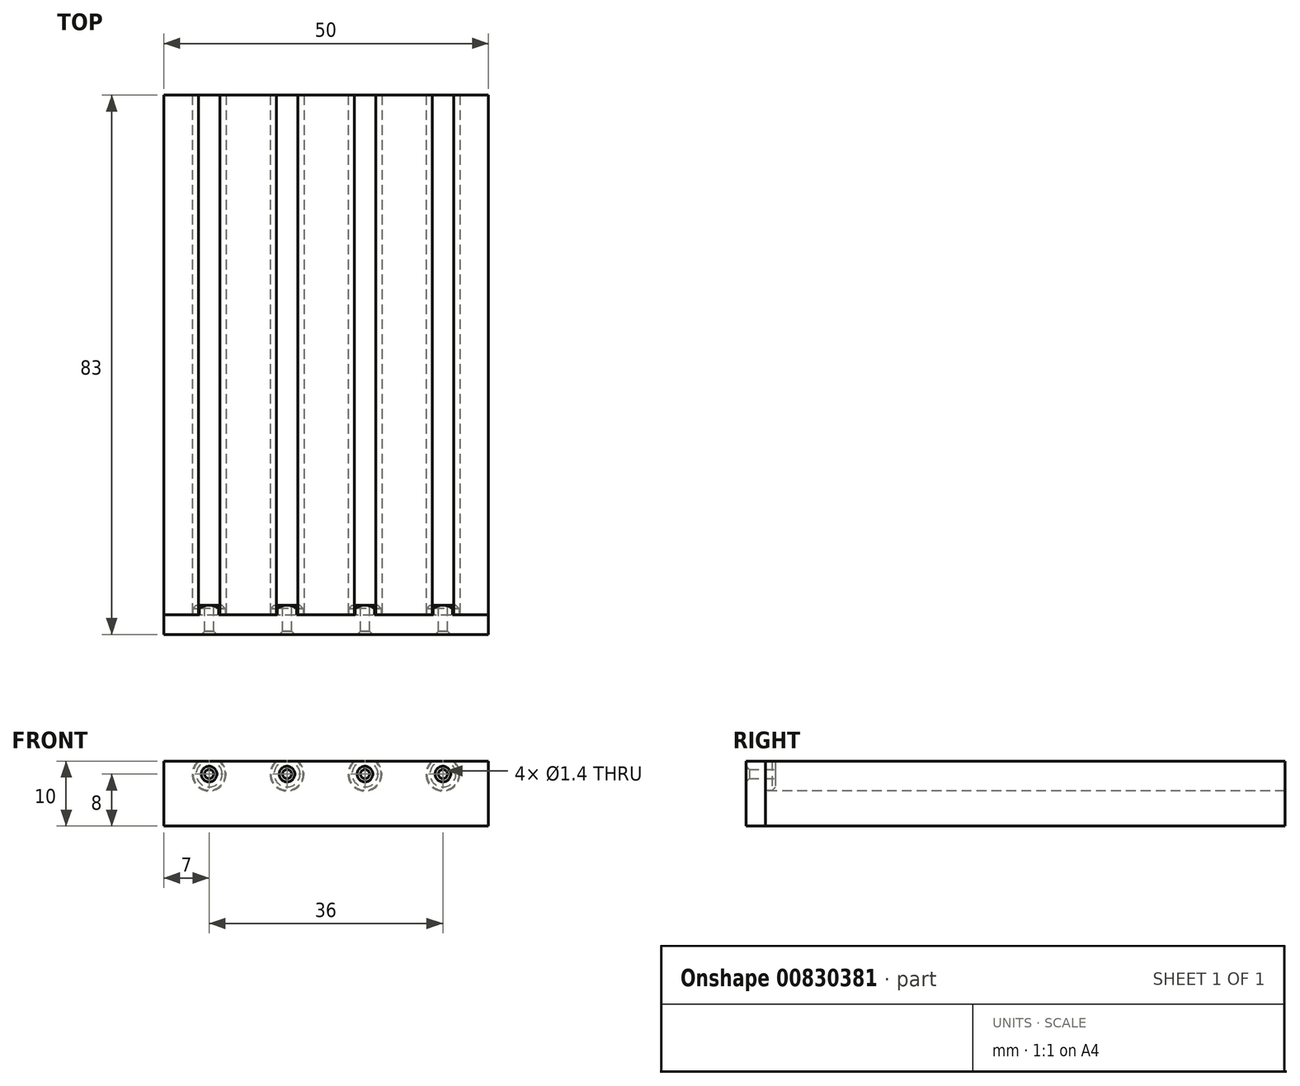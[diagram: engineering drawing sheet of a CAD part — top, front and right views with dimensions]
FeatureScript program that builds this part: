
annotation { "Feature Type Name" : "Feature", "Feature Type Description" : "" }
export const myFeature = defineFeature(function(context is Context, id is Id, definition is map)
    precondition{}
    {
        {
            var Q0;
            Q0=qCreatedBy(makeId("Top.planeOp"),FACE);
            var sketch = newSketch(context, id + "F0", { "sketchPlane" : qUnion([Q0]), "disableImprinting" : false});
            skLineSegment(sketch, "E0.bottom", {"start": v(25, 40) * mm, "end": v(-25, 40) * mm});
            skLineSegment(sketch, "E0.top", {"start": v(25, -40) * mm, "end": v(-25, -40) * mm});
            skLineSegment(sketch, "E0.left", {"start": v(25, 40) * mm, "end": v(25, -40) * mm});
            skLineSegment(sketch, "E0.right", {"start": v(-25, 40) * mm, "end": v(-25, -40) * mm});
            skPoint(sketch, "E0.middle", {"position": v(0, 0) * mm});
            skLineSegment(sketch, "E1.bottom", {"start": v(-25, -38.5) * mm, "end": v(25, -38.5) * mm});
            skLineSegment(sketch, "E1.top", {"start": v(-25, -43) * mm, "end": v(25, -43) * mm});
            skLineSegment(sketch, "E1.left", {"start": v(-25, -38.5) * mm, "end": v(-25, -43) * mm});
            skLineSegment(sketch, "E1.right", {"start": v(25, -38.5) * mm, "end": v(25, -43) * mm});
            skSolve(sketch);
        }
        {
            var Q0;
            Q0=makeQuery(id+"F0.imprint","IMPRINT",FACE,{"disambiguationData":[TD([[makeQuery(id+"F0.imprint","IMPRINT",EDGE,{"derivedFrom":sQuery(id+"F0.wireOp",EDGE,"E0.bottom")}),1.0]])]});
            var Q1;
            {var subQ0=sQuery(id+"F0.wireOp",EDGE,"E0.top");Q1=makeQuery(id+"F0.imprint","IMPRINT",FACE,{"disambiguationData":[TD([[makeQuery(id+"F0.imprint","IMPRINT",EDGE,{"derivedFrom":subQ0}),-1.0]])]});}
            extrude(context, id + "F1", {"entities" : qUnion([Q0, Q1]), "depth" : 10 * mm, "offsetDistance" : 25 * mm});
        }
        {
            var Q0;
            Q0=makeQuery(id+"F1.opExtrude","SWEPT_FACE",FACE,{"disambiguationData":[OSD([sQuery(id+"F0.wireOp",EDGE,"E0.top")])]});
            var sketch = newSketch(context, id + "F2", { "sketchPlane" : qUnion([Q0]), "disableImprinting" : false});
            skLineSegment(sketch, "E2.0.0", {"start": v(-25, 0) * mm, "end": v(25, 0) * mm});
            skLineSegment(sketch, "E2.0.1", {"start": v(25, 0) * mm, "end": v(25, 10) * mm});
            skLineSegment(sketch, "E2.0.2", {"start": v(25, 10) * mm, "end": v(-25, 10) * mm});
            skLineSegment(sketch, "E2.0.3", {"start": v(-25, 10) * mm, "end": v(-25, 0) * mm});
            skLineSegment(sketch, "E3", {"start": v(-27.18, 8) * mm, "end": v(25, 8) * mm, "construction": true});
            skCircle(sketch, "E4", {"center": v(-18, 8) * mm, "radius": 2.6 * mm});
            skCircle(sketch, "E5.1.0.0", {"center": v(-6, 8) * mm, "radius": 2.6 * mm});
            skCircle(sketch, "E5.2.0.0", {"center": v(6, 8) * mm, "radius": 2.6 * mm});
            skCircle(sketch, "E5.3.0.0", {"center": v(18, 8) * mm, "radius": 2.6 * mm});
            skLineSegment(sketch, "E5.direction1", {"start": v(-18, 8) * mm, "end": v(-6, 8) * mm, "construction": true});
            skLineSegment(sketch, "E6", {"start": v(0, 10) * mm, "end": v(0, 0) * mm, "construction": true});
            skSolve(sketch);
        }
        {
            var Q0;
            {var subQ0=sQuery(id+"F2.wireOp",EDGE,"E5.5.0.0");var subQ1=sQuery(id+"F2.wireOp",EDGE,"E2.0.2");var subQ2=makeQuery(id+"F2.imprint","INTERSECT",VERTEX,{"disambiguationData":[OD(0.0)],"derivedFrom":[subQ1,subQ0]});Q0=makeQuery(id+"F2.imprint","IMPRINT",FACE,{"disambiguationData":[TD([[makeQuery(id+"F2.imprint","IMPRINT",EDGE,{"disambiguationData":[TD([[subQ2,-1.0]])],"derivedFrom":subQ1}),-1.0]])]});}
            var Q1;
            {var subQ0=sQuery(id+"F2.wireOp",EDGE,"E5.4.0.0");var subQ1=sQuery(id+"F2.wireOp",EDGE,"E2.0.2");var subQ2=makeQuery(id+"F2.imprint","INTERSECT",VERTEX,{"disambiguationData":[OD(0.0)],"derivedFrom":[subQ1,subQ0]});Q1=makeQuery(id+"F2.imprint","IMPRINT",FACE,{"disambiguationData":[TD([[makeQuery(id+"F2.imprint","IMPRINT",EDGE,{"disambiguationData":[TD([[subQ2,-1.0]])],"derivedFrom":subQ1}),-1.0]])]});}
            var Q2;
            {var subQ0=sQuery(id+"F2.wireOp",EDGE,"E5.3.0.0");var subQ1=sQuery(id+"F2.wireOp",EDGE,"E2.0.2");var subQ2=makeQuery(id+"F2.imprint","INTERSECT",VERTEX,{"disambiguationData":[OD(0.0)],"derivedFrom":[subQ1,subQ0]});Q2=makeQuery(id+"F2.imprint","IMPRINT",FACE,{"disambiguationData":[TD([[makeQuery(id+"F2.imprint","IMPRINT",EDGE,{"disambiguationData":[TD([[subQ2,-1.0]])],"derivedFrom":subQ1}),-1.0]])]});}
            var Q3;
            {var subQ0=sQuery(id+"F2.wireOp",EDGE,"E5.2.0.0");var subQ1=sQuery(id+"F2.wireOp",EDGE,"E2.0.2");var subQ2=makeQuery(id+"F2.imprint","INTERSECT",VERTEX,{"disambiguationData":[OD(0.0)],"derivedFrom":[subQ1,subQ0]});Q3=makeQuery(id+"F2.imprint","IMPRINT",FACE,{"disambiguationData":[TD([[makeQuery(id+"F2.imprint","IMPRINT",EDGE,{"disambiguationData":[TD([[subQ2,-1.0]])],"derivedFrom":subQ1}),-1.0]])]});}
            var Q4;
            {var subQ0=sQuery(id+"F2.wireOp",EDGE,"E5.1.0.0");var subQ1=sQuery(id+"F2.wireOp",EDGE,"E2.0.2");var subQ2=makeQuery(id+"F2.imprint","INTERSECT",VERTEX,{"disambiguationData":[OD(0.0)],"derivedFrom":[subQ1,subQ0]});Q4=makeQuery(id+"F2.imprint","IMPRINT",FACE,{"disambiguationData":[TD([[makeQuery(id+"F2.imprint","IMPRINT",EDGE,{"disambiguationData":[TD([[subQ2,-1.0]])],"derivedFrom":subQ1}),-1.0]])]});}
            var Q5;
            {var subQ0=sQuery(id+"F2.wireOp",EDGE,"E4");var subQ1=sQuery(id+"F2.wireOp",EDGE,"E2.0.2");var subQ2=makeQuery(id+"F2.imprint","INTERSECT",VERTEX,{"disambiguationData":[OD(0.0)],"derivedFrom":[subQ1,subQ0]});Q5=makeQuery(id+"F2.imprint","IMPRINT",FACE,{"disambiguationData":[TD([[makeQuery(id+"F2.imprint","IMPRINT",EDGE,{"disambiguationData":[TD([[subQ2,-1.0]])],"derivedFrom":subQ1}),-1.0]])]});}
            var Q6;
            {var subQ0=sQuery(id+"F2.wireOp",EDGE,"E5.5.0.0");var subQ1=sQuery(id+"F2.wireOp",EDGE,"E2.0.2");var subQ2=makeQuery(id+"F2.imprint","INTERSECT",VERTEX,{"disambiguationData":[OD(0.0)],"derivedFrom":[subQ1,subQ0]});Q6=makeQuery(id+"F2.imprint","IMPRINT",FACE,{"disambiguationData":[TD([[makeQuery(id+"F2.imprint","IMPRINT",EDGE,{"disambiguationData":[TD([[subQ2,-1.0]])],"derivedFrom":subQ1}),1.0]])]});}
            var Q7;
            {var subQ0=sQuery(id+"F2.wireOp",EDGE,"E5.4.0.0");var subQ1=sQuery(id+"F2.wireOp",EDGE,"E2.0.2");var subQ2=makeQuery(id+"F2.imprint","INTERSECT",VERTEX,{"disambiguationData":[OD(0.0)],"derivedFrom":[subQ1,subQ0]});Q7=makeQuery(id+"F2.imprint","IMPRINT",FACE,{"disambiguationData":[TD([[makeQuery(id+"F2.imprint","IMPRINT",EDGE,{"disambiguationData":[TD([[subQ2,-1.0]])],"derivedFrom":subQ1}),1.0]])]});}
            var Q8;
            {var subQ0=sQuery(id+"F2.wireOp",EDGE,"E5.3.0.0");var subQ1=sQuery(id+"F2.wireOp",EDGE,"E2.0.2");var subQ2=makeQuery(id+"F2.imprint","INTERSECT",VERTEX,{"disambiguationData":[OD(0.0)],"derivedFrom":[subQ1,subQ0]});Q8=makeQuery(id+"F2.imprint","IMPRINT",FACE,{"disambiguationData":[TD([[makeQuery(id+"F2.imprint","IMPRINT",EDGE,{"disambiguationData":[TD([[subQ2,-1.0]])],"derivedFrom":subQ1}),1.0]])]});}
            var Q9;
            {var subQ0=sQuery(id+"F2.wireOp",EDGE,"E5.2.0.0");var subQ1=sQuery(id+"F2.wireOp",EDGE,"E2.0.2");var subQ2=makeQuery(id+"F2.imprint","INTERSECT",VERTEX,{"disambiguationData":[OD(0.0)],"derivedFrom":[subQ1,subQ0]});Q9=makeQuery(id+"F2.imprint","IMPRINT",FACE,{"disambiguationData":[TD([[makeQuery(id+"F2.imprint","IMPRINT",EDGE,{"disambiguationData":[TD([[subQ2,-1.0]])],"derivedFrom":subQ1}),1.0]])]});}
            var Q10;
            {var subQ0=sQuery(id+"F2.wireOp",EDGE,"E5.1.0.0");var subQ1=sQuery(id+"F2.wireOp",EDGE,"E2.0.2");var subQ2=makeQuery(id+"F2.imprint","INTERSECT",VERTEX,{"disambiguationData":[OD(0.0)],"derivedFrom":[subQ1,subQ0]});Q10=makeQuery(id+"F2.imprint","IMPRINT",FACE,{"disambiguationData":[TD([[makeQuery(id+"F2.imprint","IMPRINT",EDGE,{"disambiguationData":[TD([[subQ2,-1.0]])],"derivedFrom":subQ1}),1.0]])]});}
            var Q11;
            {var subQ0=sQuery(id+"F2.wireOp",EDGE,"E4");var subQ1=sQuery(id+"F2.wireOp",EDGE,"E2.0.2");var subQ2=makeQuery(id+"F2.imprint","INTERSECT",VERTEX,{"disambiguationData":[OD(0.0)],"derivedFrom":[subQ1,subQ0]});Q11=makeQuery(id+"F2.imprint","IMPRINT",FACE,{"disambiguationData":[TD([[makeQuery(id+"F2.imprint","IMPRINT",EDGE,{"disambiguationData":[TD([[subQ2,-1.0]])],"derivedFrom":subQ1}),1.0]])]});}
            var Q12;
            {var subQ0=sQuery(id+"F2.wireOp",EDGE,"1e595cce-ce77-4355-a527-9a9e8386896a.0.4.0");var subQ1=sQuery(id+"F2.wireOp",EDGE,"E2.0.2");var subQ2=makeQuery(id+"F2.imprint","INTERSECT",VERTEX,{"disambiguationData":[OD(0.0)],"derivedFrom":[subQ1,subQ0]});Q12=makeQuery(id+"F2.imprint","IMPRINT",FACE,{"disambiguationData":[TD([[makeQuery(id+"F2.imprint","IMPRINT",EDGE,{"disambiguationData":[TD([[subQ2,-1.0]])],"derivedFrom":subQ1}),1.0]])]});}
            extrude(context, id + "F3", {"entities" : qUnion([Q0, Q1, Q2, Q3, Q4, Q5, Q6, Q7, Q8, Q9, Q10, Q11, Q12]), "operationType" : NewBodyOperationType.REMOVE, "endBound" : BoundingType.THROUGH_ALL, "oppositeDirection" : true, "depth" : 25 * mm, "offsetDistance" : 25 * mm});
        }
        {
            var Q0;
            {var subQ0=sQuery(id+"F0.wireOp",EDGE,"E0.top");Q0=makeQuery(id+"F0.imprint","IMPRINT",FACE,{"disambiguationData":[TD([[makeQuery(id+"F0.imprint","IMPRINT",EDGE,{"derivedFrom":subQ0}),-1.0]])]});}
            var Q1;
            {var subQ0=sQuery(id+"F0.wireOp",EDGE,"E0.top");Q1=makeQuery(id+"F0.imprint","IMPRINT",FACE,{"disambiguationData":[TD([[makeQuery(id+"F0.imprint","IMPRINT",EDGE,{"derivedFrom":subQ0}),1.0]])]});}
            extrude(context, id + "F4", {"entities" : qUnion([Q0, Q1]), "depth" : 10 * mm, "offsetDistance" : 25 * mm});
        }
        {
            var Q0;
            Q0=makeQuery(id+"F1.opExtrude","SWEPT_BODY",BODY,{"disambiguationData":[OSD([sQuery(id+"F0.wireOp",EDGE,"E0.bottom"),sQuery(id+"F0.wireOp",EDGE,"E0.top"),sQuery(id+"F0.wireOp",EDGE,"E0.left"),sQuery(id+"F0.wireOp",EDGE,"E0.right"),sQuery(id+"F0.wireOp",EDGE,"E1.left"),sQuery(id+"F0.wireOp",EDGE,"E1.right")])]});
            var Q1;
            Q1=makeQuery(id+"F4.opExtrude","SWEPT_BODY",BODY,{"disambiguationData":[OSD([sQuery(id+"F0.wireOp",EDGE,"E1.bottom"),sQuery(id+"F0.wireOp",EDGE,"E1.top"),sQuery(id+"F0.wireOp",EDGE,"E1.left"),sQuery(id+"F0.wireOp",EDGE,"E1.right")])]});
            var Q2;
            Q2=makeQuery(id+"F4.opExtrude","SWEPT_FACE",FACE,{"disambiguationData":[OSD([sQuery(id+"F0.wireOp",EDGE,"E1.bottom")])]});
            var Q3;
            Q3=makeQuery(id+"F3.boolean.opBoolean","COPY",FACE,{"derivedFrom":makeQuery(id+"F3.opExtrude","SWEPT_FACE",FACE,{"disambiguationData":[OSD([sQuery(id+"F2.wireOp",EDGE,"E5.2.0.0")])]})});
            var Q4;
            Q4=makeQuery(id+"F3.boolean.opBoolean","COPY",FACE,{"derivedFrom":makeQuery(id+"F3.opExtrude","SWEPT_FACE",FACE,{"disambiguationData":[OSD([sQuery(id+"F2.wireOp",EDGE,"E5.3.0.0")])]})});
            var Q5;
            Q5=makeQuery(id+"F3.boolean.opBoolean","COPY",FACE,{"derivedFrom":makeQuery(id+"F3.opExtrude","SWEPT_FACE",FACE,{"disambiguationData":[OSD([sQuery(id+"F2.wireOp",EDGE,"E5.1.0.0")])]})});
            var Q6;
            Q6=makeQuery(id+"F3.boolean.opBoolean","COPY",FACE,{"derivedFrom":makeQuery(id+"F3.opExtrude","SWEPT_FACE",FACE,{"disambiguationData":[OSD([sQuery(id+"F2.wireOp",EDGE,"E4")])]})});
            booleanBodies(context, id + "F5", {"operationType" : BooleanOperationType.SUBTRACTION, "tools" : qUnion([Q0]), "targets" : qUnion([Q1]), "offset" : true, "entitiesToOffset" : qUnion([Q2, Q3, Q4, Q5, Q6]), "offsetDistance" : .1 * mm, "keepTools" : true});
        }
        {
            var Q0;
            {var subQ0=sQuery(id+"F0.wireOp",EDGE,"E1.bottom");Q0=makeQuery(id+"F5.opBoolean","SPLIT",FACE,{"disambiguationData":[TD([makeQuery(id+"F3.boolean.opBoolean","COPY",FACE,{"derivedFrom":makeQuery(id+"F3.opExtrude","SWEPT_FACE",FACE,{"disambiguationData":[OSD([sQuery(id+"F2.wireOp",EDGE,"E4")])]})})])],"derivedFrom":makeQuery(id+"F4.opExtrude","SWEPT_FACE",FACE,{"disambiguationData":[OSD([subQ0])]})});}
            var sketch = newSketch(context, id + "F6", { "sketchPlane" : qUnion([Q0])});
            skCircle(sketch, "E7", {"center": v(18, 8) * mm, "radius": 0.7 * mm});
            skCircle(sketch, "E8.1.0.0", {"center": v(6, 8) * mm, "radius": 0.7 * mm});
            skCircle(sketch, "E8.2.0.0", {"center": v(-6, 8) * mm, "radius": 0.7 * mm});
            skCircle(sketch, "E8.3.0.0", {"center": v(-18, 8) * mm, "radius": 0.7 * mm});
            skLineSegment(sketch, "E8.direction1", {"start": v(18, 8) * mm, "end": v(6, 8) * mm, "construction": true});
            skSolve(sketch);
        }
        {
            var Q0;
            Q0=makeQuery(id+"F6.imprint","IMPRINT",FACE,{"disambiguationData":[TD([[makeQuery(id+"F6.imprint","IMPRINT",EDGE,{"derivedFrom":sQuery(id+"F6.wireOp",EDGE,"E7")}),1.0]])]});
            var Q1;
            Q1=makeQuery(id+"F6.imprint","IMPRINT",FACE,{"disambiguationData":[TD([[makeQuery(id+"F6.imprint","IMPRINT",EDGE,{"derivedFrom":sQuery(id+"F6.wireOp",EDGE,"E8.1.0.0")}),1.0]])]});
            var Q2;
            Q2=makeQuery(id+"F6.imprint","IMPRINT",FACE,{"disambiguationData":[TD([[makeQuery(id+"F6.imprint","IMPRINT",EDGE,{"derivedFrom":sQuery(id+"F6.wireOp",EDGE,"E8.2.0.0")}),1.0]])]});
            var Q3;
            Q3=makeQuery(id+"F6.imprint","IMPRINT",FACE,{"disambiguationData":[TD([[makeQuery(id+"F6.imprint","IMPRINT",EDGE,{"derivedFrom":sQuery(id+"F6.wireOp",EDGE,"E8.3.0.0")}),1.0]])]});
            var Q4;
            Q4=makeQuery(id+"F6.imprint","IMPRINT",FACE,{"disambiguationData":[TD([[makeQuery(id+"F6.imprint","IMPRINT",EDGE,{"derivedFrom":sQuery(id+"F6.wireOp",EDGE,"E8.4.0.0")}),1.0]])]});
            extrude(context, id + "F7", {"entities" : qUnion([Q0, Q1, Q2, Q3, Q4]), "operationType" : NewBodyOperationType.REMOVE, "oppositeDirection" : true, "depth" : 25 * mm, "offsetDistance" : 25 * mm});
        }
        {
            var Q0;
            Q0=makeQuery(id+"F5.tempBoolean.opBoolean","INTERSECT",EDGE,{"derivedFrom":[makeQuery(id+"F4.opExtrude","SWEPT_FACE",FACE,{"disambiguationData":[OSD([sQuery(id+"F0.wireOp",EDGE,"E1.bottom")])]}),makeQuery(id+"F5.offsetTempBody.opPattern","COPY",FACE,{"derivedFrom":makeQuery(id+"F3.boolean.opBoolean","COPY",FACE,{"derivedFrom":makeQuery(id+"F3.opExtrude","SWEPT_FACE",FACE,{"disambiguationData":[OSD([sQuery(id+"F2.wireOp",EDGE,"E5.1.0.0")])]})}),"instanceName":"1"})]});
            var Q1;
            Q1=makeQuery(id+"F5.tempBoolean.opBoolean","INTERSECT",EDGE,{"derivedFrom":[makeQuery(id+"F4.opExtrude","SWEPT_FACE",FACE,{"disambiguationData":[OSD([sQuery(id+"F0.wireOp",EDGE,"E1.bottom")])]}),makeQuery(id+"F5.offsetTempBody.opPattern","COPY",FACE,{"derivedFrom":makeQuery(id+"F3.boolean.opBoolean","COPY",FACE,{"derivedFrom":makeQuery(id+"F3.opExtrude","SWEPT_FACE",FACE,{"disambiguationData":[OSD([sQuery(id+"F2.wireOp",EDGE,"E4")])]})}),"instanceName":"1"})]});
            var Q2;
            Q2=makeQuery(id+"F5.tempBoolean.opBoolean","INTERSECT",EDGE,{"derivedFrom":[makeQuery(id+"F4.opExtrude","SWEPT_FACE",FACE,{"disambiguationData":[OSD([sQuery(id+"F0.wireOp",EDGE,"E1.bottom")])]}),makeQuery(id+"F5.offsetTempBody.opPattern","COPY",FACE,{"derivedFrom":makeQuery(id+"F3.boolean.opBoolean","COPY",FACE,{"derivedFrom":makeQuery(id+"F3.opExtrude","SWEPT_FACE",FACE,{"disambiguationData":[OSD([sQuery(id+"F2.wireOp",EDGE,"E5.2.0.0")])]})}),"instanceName":"1"})]});
            var Q3;
            Q3=makeQuery(id+"F5.tempBoolean.opBoolean","INTERSECT",EDGE,{"derivedFrom":[makeQuery(id+"F4.opExtrude","SWEPT_FACE",FACE,{"disambiguationData":[OSD([sQuery(id+"F0.wireOp",EDGE,"E1.bottom")])]}),makeQuery(id+"F5.offsetTempBody.opPattern","COPY",FACE,{"derivedFrom":makeQuery(id+"F3.boolean.opBoolean","COPY",FACE,{"derivedFrom":makeQuery(id+"F3.opExtrude","SWEPT_FACE",FACE,{"disambiguationData":[OSD([sQuery(id+"F2.wireOp",EDGE,"E5.3.0.0")])]})}),"instanceName":"1"})]});
            var Q4;
            Q4=makeQuery(id+"F7.boolean.opBoolean","INTERSECT",EDGE,{"derivedFrom":[makeQuery(id+"F4.opExtrude","SWEPT_FACE",FACE,{"disambiguationData":[OSD([sQuery(id+"F0.wireOp",EDGE,"E1.top")])]}),makeQuery(id+"F7.opExtrude","SWEPT_FACE",FACE,{"disambiguationData":[OSD([sQuery(id+"F6.wireOp",EDGE,"E7")])]})]});
            var Q5;
            Q5=makeQuery(id+"F7.boolean.opBoolean","INTERSECT",EDGE,{"derivedFrom":[makeQuery(id+"F4.opExtrude","SWEPT_FACE",FACE,{"disambiguationData":[OSD([sQuery(id+"F0.wireOp",EDGE,"E1.top")])]}),makeQuery(id+"F7.opExtrude","SWEPT_FACE",FACE,{"disambiguationData":[OSD([sQuery(id+"F6.wireOp",EDGE,"E8.1.0.0")])]})]});
            var Q6;
            Q6=makeQuery(id+"F7.boolean.opBoolean","INTERSECT",EDGE,{"derivedFrom":[makeQuery(id+"F4.opExtrude","SWEPT_FACE",FACE,{"disambiguationData":[OSD([sQuery(id+"F0.wireOp",EDGE,"E1.top")])]}),makeQuery(id+"F7.opExtrude","SWEPT_FACE",FACE,{"disambiguationData":[OSD([sQuery(id+"F6.wireOp",EDGE,"E8.2.0.0")])]})]});
            var Q7;
            Q7=makeQuery(id+"F7.boolean.opBoolean","COPY",EDGE,{"derivedFrom":makeQuery(id+"F7.opExtrude","CAP_EDGE",EDGE,{"disambiguationData":[OSD([sQuery(id+"F6.wireOp",EDGE,"E8.3.0.0")])],"isStart":true})});
            var Q8;
            Q8=makeQuery(id+"F7.boolean.opBoolean","INTERSECT",EDGE,{"derivedFrom":[makeQuery(id+"F4.opExtrude","SWEPT_FACE",FACE,{"disambiguationData":[OSD([sQuery(id+"F0.wireOp",EDGE,"E1.top")])]}),makeQuery(id+"F7.opExtrude","SWEPT_FACE",FACE,{"disambiguationData":[OSD([sQuery(id+"F6.wireOp",EDGE,"E8.3.0.0")])]})]});
            var Q9;
            Q9=makeQuery(id+"F7.boolean.opBoolean","COPY",EDGE,{"derivedFrom":makeQuery(id+"F7.opExtrude","CAP_EDGE",EDGE,{"disambiguationData":[OSD([sQuery(id+"F6.wireOp",EDGE,"E8.2.0.0")])],"isStart":true})});
            var Q10;
            Q10=makeQuery(id+"F7.boolean.opBoolean","COPY",EDGE,{"derivedFrom":makeQuery(id+"F7.opExtrude","CAP_EDGE",EDGE,{"disambiguationData":[OSD([sQuery(id+"F6.wireOp",EDGE,"E8.1.0.0")])],"isStart":true})});
            var Q11;
            Q11=makeQuery(id+"F7.boolean.opBoolean","COPY",EDGE,{"derivedFrom":makeQuery(id+"F7.opExtrude","CAP_EDGE",EDGE,{"disambiguationData":[OSD([sQuery(id+"F6.wireOp",EDGE,"E7")])],"isStart":true})});
            chamfer(context, id + "F8", {"entities" : qUnion([Q0, Q1, Q2, Q3, Q4, Q5, Q6, Q7, Q8, Q9, Q10, Q11]), "width" : .5 * mm});
        }
    });
